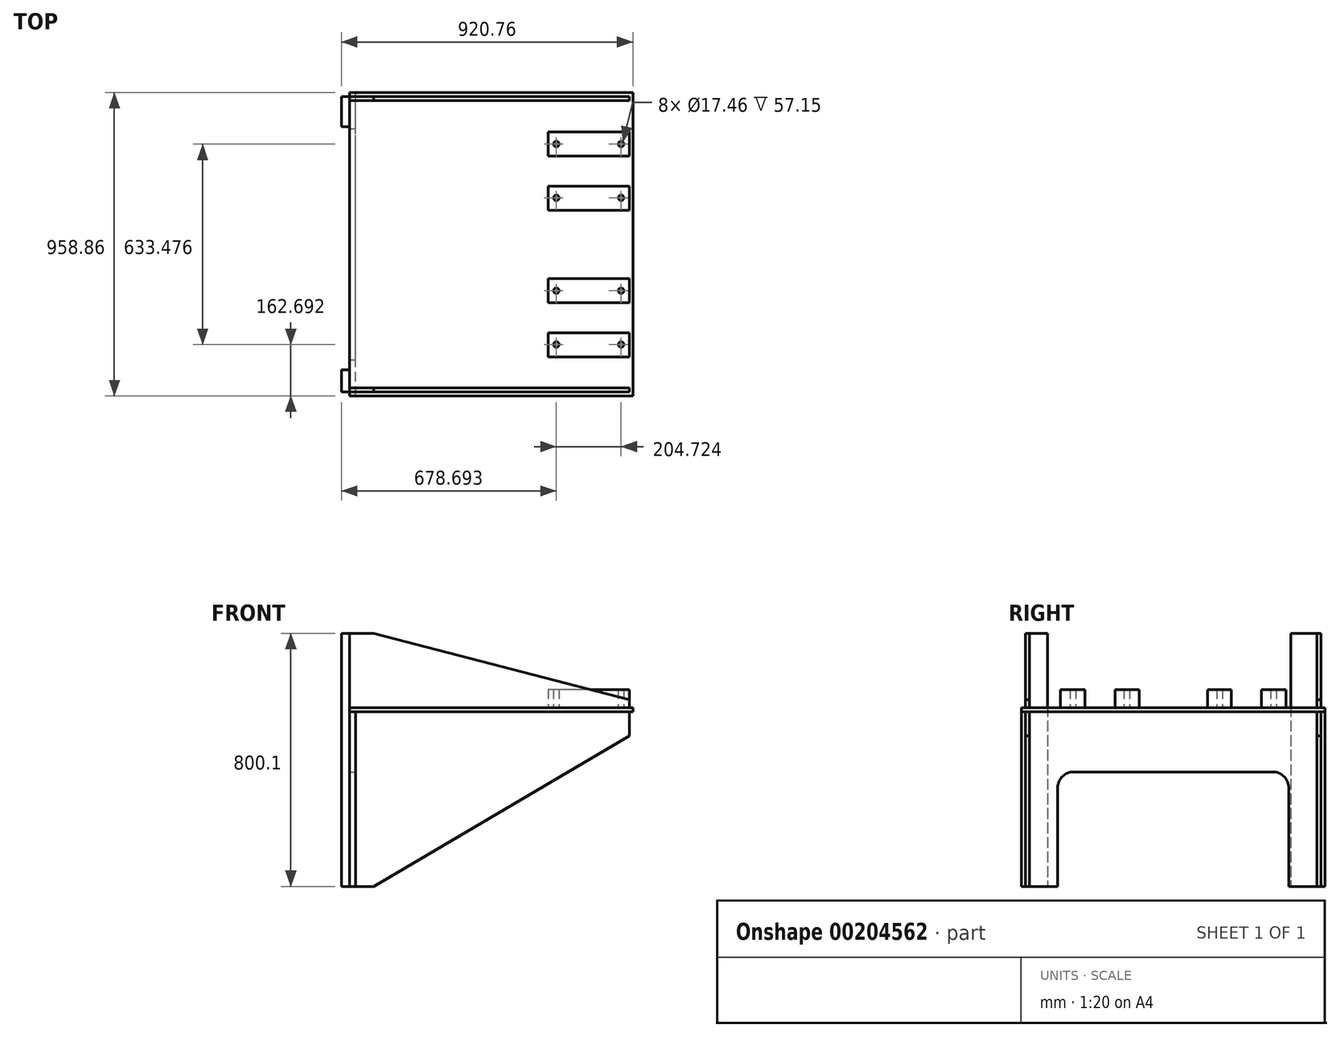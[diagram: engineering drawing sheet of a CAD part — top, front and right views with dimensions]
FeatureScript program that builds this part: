
annotation { "Feature Type Name" : "Feature", "Feature Type Description" : "" }
export const myFeature = defineFeature(function(context is Context, id is Id, definition is map)
    precondition{}
    {
        {
            var Q0;
            Q0=qCreatedBy(makeId("Top.planeOp"),FACE);
            var sketch = newSketch(context, id + "F0", { "sketchPlane" : qUnion([Q0])});
            skLineSegment(sketch, "E0.bottom", {"start": v(-447.67, 479.42) * mm, "end": v(447.68, 479.42) * mm});
            skLineSegment(sketch, "E0.top", {"start": v(-447.68, -479.43) * mm, "end": v(447.68, -479.43) * mm});
            skLineSegment(sketch, "E0.left", {"start": v(-447.67, 479.42) * mm, "end": v(-447.68, -479.43) * mm});
            skLineSegment(sketch, "E0.right", {"start": v(447.68, 479.42) * mm, "end": v(447.68, -479.43) * mm});
            skPoint(sketch, "E0.middle", {"position": v(0, 0) * mm});
            skSolve(sketch);
        }
        {
            var Q0;
            Q0 = qSketchRegion(id + "F0", true);
            extrude(context, id + "F1", {"entities" : qUnion([Q0]), "depth" : 12.7 * mm});
        }
        {
            var Q0;
            Q0=makeQuery(id+"F1.opExtrude","CAP_FACE",FACE,{"disambiguationData":[OSD([sQuery(id+"F0.wireOp",EDGE,"E0.bottom"),sQuery(id+"F0.wireOp",EDGE,"E0.top"),sQuery(id+"F0.wireOp",EDGE,"E0.left"),sQuery(id+"F0.wireOp",EDGE,"E0.right")])],"isStart":false});
            var sketch = newSketch(context, id + "F2", { "sketchPlane" : qUnion([Q0])});
            skLineSegment(sketch, "E1", {"start": v(-672.74, 0) * mm, "end": v(646.91, 0) * mm, "construction": true});
            skPoint(sketch, "E1.endSnap0", {"position": v(-447.68, 0) * mm});
            skLineSegment(sketch, "E2.0", {"start": v(447.68, 479.42) * mm, "end": v(447.68, -479.43) * mm, "construction": true});
            skLineSegment(sketch, "E3.0", {"start": v(436.5, 479.42) * mm, "end": v(436.5, -479.43) * mm, "construction": true});
            skLineSegment(sketch, "E4.0", {"start": v(-672.74, -107.95) * mm, "end": v(646.91, -107.95) * mm, "construction": true});
            skLineSegment(sketch, "E5.0", {"start": v(-672.74, -184.15) * mm, "end": v(646.91, -184.15) * mm, "construction": true});
            skLineSegment(sketch, "E6.0", {"start": v(-672.74, -279.4) * mm, "end": v(646.91, -279.4) * mm, "construction": true});
            skLineSegment(sketch, "E7.0", {"start": v(-672.74, -355.6) * mm, "end": v(646.91, -355.6) * mm, "construction": true});
            skLineSegment(sketch, "E8.bottom", {"start": v(436.5, -107.95) * mm, "end": v(179.45, -107.95) * mm});
            skLineSegment(sketch, "E8.top", {"start": v(436.5, -184.15) * mm, "end": v(179.45, -184.15) * mm});
            skLineSegment(sketch, "E8.left", {"start": v(436.5, -107.95) * mm, "end": v(436.5, -184.15) * mm});
            skLineSegment(sketch, "E8.right", {"start": v(179.45, -107.95) * mm, "end": v(179.45, -184.15) * mm});
            skLineSegment(sketch, "E9.bottom", {"start": v(436.5, -279.4) * mm, "end": v(179.45, -279.4) * mm});
            skLineSegment(sketch, "E9.top", {"start": v(436.5, -355.6) * mm, "end": v(179.45, -355.6) * mm});
            skLineSegment(sketch, "E9.left", {"start": v(436.5, -279.4) * mm, "end": v(436.5, -355.6) * mm});
            skLineSegment(sketch, "E9.right", {"start": v(179.45, -279.4) * mm, "end": v(179.45, -355.6) * mm});
            skLineSegment(sketch, "E10.0", {"start": v(-672.74, -146.81) * mm, "end": v(646.91, -146.81) * mm, "construction": true});
            skLineSegment(sketch, "E11.0", {"start": v(-672.74, -316.74) * mm, "end": v(646.91, -316.74) * mm, "construction": true});
            skLineSegment(sketch, "E12", {"start": v(307.98, -107.95) * mm, "end": v(307.98, -355.6) * mm, "construction": true});
            skLineSegment(sketch, "E13.0", {"start": v(205.61, -107.95) * mm, "end": v(205.61, -355.6) * mm, "construction": true});
            skCircle(sketch, "E14", {"center": v(205.61, -146.81) * mm, "radius": 8.73 * mm});
            skCircle(sketch, "E15", {"center": v(205.61, -316.74) * mm, "radius": 8.73 * mm});
            skCircle(sketch, "E16.MirrorC", {"center": v(410.34, -146.81) * mm, "radius": 8.73 * mm});
            skCircle(sketch, "E17.MirrorC", {"center": v(410.34, -316.74) * mm, "radius": 8.73 * mm});
            skLineSegment(sketch, "E18.MirrorCS", {"start": v(205.61, 107.95) * mm, "end": v(205.61, 355.6) * mm, "construction": true});
            skLineSegment(sketch, "E19.MirrorCS", {"start": v(307.98, 107.95) * mm, "end": v(307.98, 355.6) * mm, "construction": true});
            skLineSegment(sketch, "E20.MirrorCS", {"start": v(436.5, 107.95) * mm, "end": v(179.45, 107.95) * mm});
            skLineSegment(sketch, "E21.MirrorCS", {"start": v(436.5, 184.15) * mm, "end": v(179.45, 184.15) * mm});
            skCircle(sketch, "E22.MirrorC", {"center": v(410.34, 316.74) * mm, "radius": 8.73 * mm});
            skLineSegment(sketch, "E23.MirrorCS", {"start": v(436.5, 107.95) * mm, "end": v(436.5, 184.15) * mm});
            skLineSegment(sketch, "E24.MirrorCS", {"start": v(179.45, 107.95) * mm, "end": v(179.45, 184.15) * mm});
            skCircle(sketch, "E25.MirrorC", {"center": v(205.61, 146.81) * mm, "radius": 8.73 * mm});
            skCircle(sketch, "E26.MirrorC", {"center": v(410.34, 146.81) * mm, "radius": 8.73 * mm});
            skLineSegment(sketch, "E27.MirrorCS", {"start": v(436.5, 279.4) * mm, "end": v(179.45, 279.4) * mm});
            skLineSegment(sketch, "E28.MirrorCS", {"start": v(436.5, 279.4) * mm, "end": v(436.5, 355.6) * mm});
            skLineSegment(sketch, "E29.MirrorCS", {"start": v(436.5, 355.6) * mm, "end": v(179.45, 355.6) * mm});
            skCircle(sketch, "E30.MirrorC", {"center": v(205.61, 316.74) * mm, "radius": 8.73 * mm});
            skLineSegment(sketch, "E31.MirrorCS", {"start": v(179.45, 279.4) * mm, "end": v(179.45, 355.6) * mm});
            skSolve(sketch);
        }
        {
            var Q0;
            Q0 = qSketchRegion(id + "F2", true);
            extrude(context, id + "F3", {"entities" : qUnion([Q0]), "operationType" : NewBodyOperationType.ADD, "depth" : 57.15 * mm});
        }
        {
            var Q0;
            Q0=qCreatedBy(makeId("Front.planeOp"),FACE);
            cPlane(context, id + "F4", {"entities" : qUnion([Q0]), "cplaneType" : CPlaneType.OFFSET, "offset" : 454.15 * mm, "width" : 152.4 * mm, "height" : 152.4 * mm});
        }
        {
            var Q0;
            Q0=qCreatedBy(id+"F4.planeOp",FACE);
            var sketch = newSketch(context, id + "F5", { "sketchPlane" : qUnion([Q0])});
            skLineSegment(sketch, "E32.0", {"start": v(436.5, 69.85) * mm, "end": v(436.5, 12.7) * mm, "construction": true});
            skLineSegment(sketch, "E33.0", {"start": v(-447.68, 12.7) * mm, "end": v(447.68, 12.7) * mm, "construction": true});
            skLineSegment(sketch, "E34.bottom", {"start": v(-447.68, 12.7) * mm, "end": v(436.5, 12.7) * mm});
            skLineSegment(sketch, "E34.top", {"start": v(-447.68, 247.65) * mm, "end": v(-371.48, 247.65) * mm});
            skLineSegment(sketch, "E34.left", {"start": v(-447.68, 12.7) * mm, "end": v(-447.68, 247.65) * mm});
            skLineSegment(sketch, "E34.right", {"start": v(436.5, 12.7) * mm, "end": v(436.5, 69.85) * mm});
            skLineSegment(sketch, "E35.0", {"start": v(-371.48, 12.7) * mm, "end": v(-371.48, 247.65) * mm, "construction": true});
            skLineSegment(sketch, "E36.0", {"start": v(-447.68, 38.1) * mm, "end": v(436.5, 38.1) * mm, "construction": true});
            skLineSegment(sketch, "E37", {"start": v(-371.48, 247.65) * mm, "end": v(436.5, 38.1) * mm});
            skPoint(sketch, "E38.orphan", {"position": v(436.5, 247.65) * mm});
            skSolve(sketch);
        }
        {
            var Q0;
            Q0 = qSketchRegion(id + "F5", true);
            extrude(context, id + "F6", {"entities" : qUnion([Q0]), "depth" : 12.7 * mm});
        }
        {
            var Q0;
            Q0=makeQuery(id+"F6.opExtrude","CAP_FACE",FACE,{"disambiguationData":[OSD([sQuery(id+"F5.wireOp",EDGE,"E34.bottom"),sQuery(id+"F5.wireOp",EDGE,"E34.top"),sQuery(id+"F5.wireOp",EDGE,"E34.left"),sQuery(id+"F5.wireOp",EDGE,"E34.right"),sQuery(id+"F5.wireOp",EDGE,"E37")])],"isStart":false});
            var sketch = newSketch(context, id + "F7", { "sketchPlane" : qUnion([Q0])});
            skLineSegment(sketch, "E39.0", {"start": v(436.5, 0) * mm, "end": v(436.5, 38.1) * mm, "construction": true});
            skLineSegment(sketch, "E40.0", {"start": v(-447.68, 0) * mm, "end": v(447.68, 0) * mm, "construction": true});
            skPoint(sketch, "E41.orphan", {"position": v(436.5, 12.7) * mm});
            skLineSegment(sketch, "E42.0", {"start": v(-447.68, 12.7) * mm, "end": v(-447.68, 0) * mm, "construction": true});
            skLineSegment(sketch, "E43.bottom", {"start": v(436.5, 0) * mm, "end": v(-447.68, 0) * mm});
            skLineSegment(sketch, "E43.top", {"start": v(-371.48, -552.45) * mm, "end": v(-447.68, -552.45) * mm});
            skLineSegment(sketch, "E43.left", {"start": v(436.5, 0) * mm, "end": v(436.5, -76.2) * mm});
            skLineSegment(sketch, "E43.right", {"start": v(-447.68, 0) * mm, "end": v(-447.68, -552.45) * mm});
            skLineSegment(sketch, "E44.0", {"start": v(-371.48, 0) * mm, "end": v(-371.47, -552.45) * mm, "construction": true});
            skLineSegment(sketch, "E45.0", {"start": v(-447.68, -76.2) * mm, "end": v(436.5, -76.2) * mm, "construction": true});
            skLineSegment(sketch, "E46", {"start": v(-371.47, -552.45) * mm, "end": v(436.5, -76.2) * mm});
            skSolve(sketch);
        }
        {
            var Q0;
            Q0 = qSketchRegion(id + "F7", true);
            extrude(context, id + "F8", {"entities" : qUnion([Q0]), "oppositeDirection" : true, "depth" : 12.7 * mm});
        }
        {
            var Q0;
            Q0=makeQuery(id+"F8.opExtrude","CAP_FACE",FACE,{"disambiguationData":[OSD([sQuery(id+"F7.wireOp",EDGE,"E43.bottom"),sQuery(id+"F7.wireOp",EDGE,"E43.top"),sQuery(id+"F7.wireOp",EDGE,"E43.left"),sQuery(id+"F7.wireOp",EDGE,"E43.right"),sQuery(id+"F7.wireOp",EDGE,"E46")])],"isStart":true});
            var sketch = newSketch(context, id + "F9", { "sketchPlane" : qUnion([Q0])});
            skLineSegment(sketch, "E47.bottom", {"start": v(-447.68, -552.45) * mm, "end": v(-428.63, -552.45) * mm});
            skLineSegment(sketch, "E47.top", {"start": v(-447.68, 0) * mm, "end": v(-428.63, 0) * mm});
            skLineSegment(sketch, "E47.left", {"start": v(-447.68, -552.45) * mm, "end": v(-447.68, 0) * mm});
            skLineSegment(sketch, "E47.right", {"start": v(-428.63, -552.45) * mm, "end": v(-428.63, 0) * mm});
            skSolve(sketch);
        }
        {
            var Q0;
            Q0 = qSketchRegion(id + "F9", true);
            extrude(context, id + "F10", {"entities" : qUnion([Q0]), "operationType" : NewBodyOperationType.REMOVE, "endBound" : BoundingType.THROUGH_ALL, "oppositeDirection" : true, "depth" : 25.4 * mm});
        }
        {
            var Q0;
            Q0=makeQuery(id+"F6.opExtrude","SWEPT_BODY",BODY,{"disambiguationData":[OSD([sQuery(id+"F5.wireOp",EDGE,"E34.bottom"),sQuery(id+"F5.wireOp",EDGE,"E34.top"),sQuery(id+"F5.wireOp",EDGE,"E34.left"),sQuery(id+"F5.wireOp",EDGE,"E34.right"),sQuery(id+"F5.wireOp",EDGE,"E37")])]});
            var Q1;
            Q1=makeQuery(id+"F8.opExtrude","SWEPT_BODY",BODY,{"disambiguationData":[OSD([sQuery(id+"F7.wireOp",EDGE,"E43.bottom"),sQuery(id+"F7.wireOp",EDGE,"E43.top"),sQuery(id+"F7.wireOp",EDGE,"E43.left"),sQuery(id+"F7.wireOp",EDGE,"E43.right"),sQuery(id+"F7.wireOp",EDGE,"E46")])]});
            var Q2;
            Q2=qCreatedBy(makeId("Front.planeOp"),FACE);
            mirror(context, id + "F11", {"entities" : qUnion([Q0, Q1]), "mirrorPlane" : qUnion([Q2])});
        }
        {
            var Q0;
            Q0=makeQuery(id+"F10.boolean.opBoolean","COPY",FACE,{"derivedFrom":makeQuery(id+"F10.opExtrude","SWEPT_FACE",FACE,{"disambiguationData":[OSD([sQuery(id+"F9.wireOp",EDGE,"E47.right")])]})});
            var sketch = newSketch(context, id + "F12", { "sketchPlane" : qUnion([Q0])});
            skLineSegment(sketch, "E48.0", {"start": v(-479.42, 0) * mm, "end": v(479.43, 0) * mm, "construction": true});
            skLineSegment(sketch, "E49.0", {"start": v(-454.15, -552.45) * mm, "end": v(-466.85, -552.45) * mm, "construction": true});
            skLineSegment(sketch, "E50.bottom", {"start": v(479.43, 0) * mm, "end": v(-479.42, 0) * mm});
            skLineSegment(sketch, "E50.top", {"start": v(479.43, -552.45) * mm, "end": v(365.13, -552.45) * mm});
            skLineSegment(sketch, "E50.left", {"start": v(479.43, 0) * mm, "end": v(479.43, -552.45) * mm});
            skLineSegment(sketch, "E50.right", {"start": v(-479.42, 0) * mm, "end": v(-479.42, -552.45) * mm});
            skLineSegment(sketch, "E51", {"start": v(0, -634.58) * mm, "end": v(0, -170.12) * mm, "construction": true});
            skLineSegment(sketch, "E52.0", {"start": v(365.13, -634.58) * mm, "end": v(365.13, -241.3) * mm, "construction": true});
            skLineSegment(sketch, "E53.0", {"start": v(314.33, -190.5) * mm, "end": v(-314.33, -190.5) * mm});
            skLineSegment(sketch, "E54.left", {"start": v(365.13, -190.5) * mm, "end": v(365.13, -647.7) * mm});
            skLineSegment(sketch, "E54.right", {"start": v(-365.13, -241.3) * mm, "end": v(-365.12, -647.7) * mm});
            skArc(sketch, "E55.filletArc", {"start": v(-314.33, -190.5) * mm, "mid": v(-350.25, -205.38) * mm, "end": v(-365.13, -241.3) * mm});
            skPoint(sketch, "E56.visualSharp", {"position": v(365.13, -190.5) * mm});
            skArc(sketch, "E56.filletArc", {"start": v(365.13, -241.3) * mm, "mid": v(350.25, -205.38) * mm, "end": v(314.33, -190.5) * mm});
            skLineSegment(sketch, "E57.trimOffspring", {"start": v(0, -552.45) * mm, "end": v(-479.42, -552.45) * mm});
            skSolve(sketch);
        }
        {
            var Q0;
            Q0 = qSketchRegion(id + "F12", true);
            extrude(context, id + "F13", {"entities" : qUnion([Q0]), "depth" : 19.05 * mm});
        }
        {
            var Q0;
            Q0=makeQuery(id+"F13.opExtrude","CAP_FACE",FACE,{"disambiguationData":[OSD([sQuery(id+"F12.wireOp",EDGE,"E50.bottom"),sQuery(id+"F12.wireOp",EDGE,"E50.top"),sQuery(id+"F12.wireOp",EDGE,"E50.left"),sQuery(id+"F12.wireOp",EDGE,"E50.right"),sQuery(id+"F12.wireOp",EDGE,"E53.0"),sQuery(id+"F12.wireOp",EDGE,"E54.left"),sQuery(id+"F12.wireOp",EDGE,"E54.right"),sQuery(id+"F12.wireOp",EDGE,"E55.filletArc"),sQuery(id+"F12.wireOp",EDGE,"E56.filletArc"),sQuery(id+"F12.wireOp",EDGE,"E57.trimOffspring")])],"isStart":false});
            var sketch = newSketch(context, id + "F14", { "sketchPlane" : qUnion([Q0])});
            skLineSegment(sketch, "E58.0", {"start": v(466.85, 12.7) * mm, "end": v(466.85, 247.65) * mm, "construction": true});
            skLineSegment(sketch, "E59.0", {"start": v(-466.85, 12.7) * mm, "end": v(-466.85, 247.65) * mm, "construction": true});
            skLineSegment(sketch, "E60.0", {"start": v(-365.13, -552.45) * mm, "end": v(-479.42, -552.45) * mm, "construction": true});
            skLineSegment(sketch, "E61.0", {"start": v(479.43, -552.45) * mm, "end": v(365.13, -552.45) * mm, "construction": true});
            skLineSegment(sketch, "E62.bottom", {"start": v(466.85, 247.65) * mm, "end": v(397, 247.65) * mm});
            skLineSegment(sketch, "E62.top", {"start": v(466.85, -552.45) * mm, "end": v(397, -552.45) * mm});
            skLineSegment(sketch, "E62.left", {"start": v(466.85, 247.65) * mm, "end": v(466.85, -552.45) * mm});
            skLineSegment(sketch, "E62.right", {"start": v(397, 247.65) * mm, "end": v(397, -552.45) * mm});
            skLineSegment(sketch, "E63.bottom", {"start": v(-466.85, 247.65) * mm, "end": v(-371.6, 247.65) * mm});
            skLineSegment(sketch, "E63.top", {"start": v(-466.85, -552.45) * mm, "end": v(-371.6, -552.45) * mm});
            skLineSegment(sketch, "E63.left", {"start": v(-466.85, 247.65) * mm, "end": v(-466.85, -552.45) * mm});
            skLineSegment(sketch, "E63.right", {"start": v(-371.6, 247.65) * mm, "end": v(-371.6, -552.45) * mm});
            skSolve(sketch);
        }
        {
            var Q0;
            Q0 = qSketchRegion(id + "F14", true);
            extrude(context, id + "F15", {"entities" : qUnion([Q0]), "depth" : 25.4 * mm});
        }
    });
